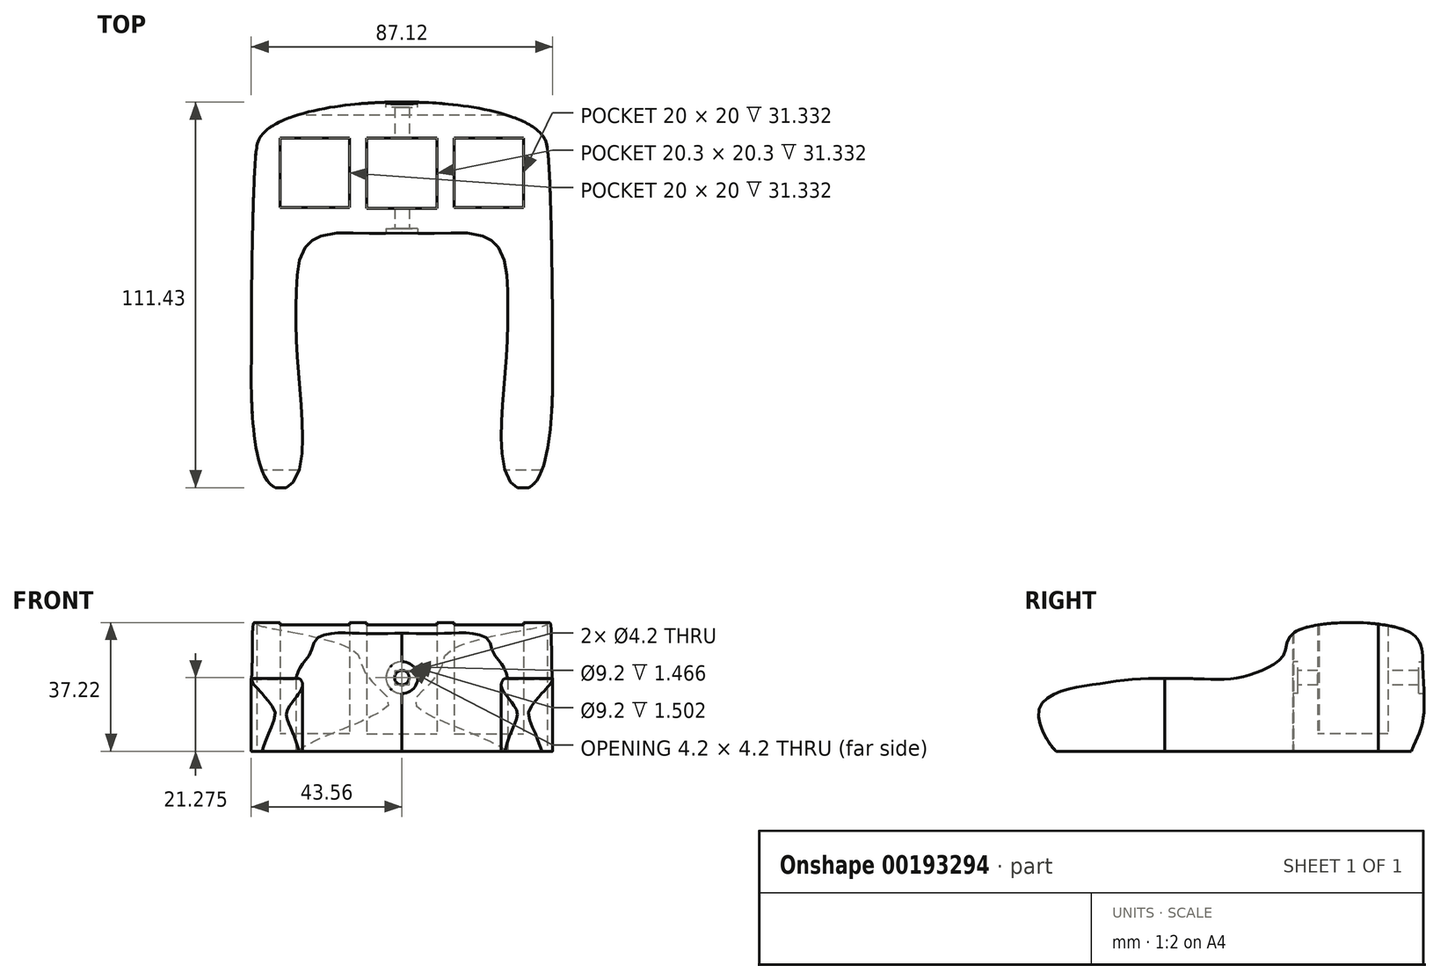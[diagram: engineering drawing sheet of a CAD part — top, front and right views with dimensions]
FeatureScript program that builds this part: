
annotation { "Feature Type Name" : "Feature", "Feature Type Description" : "" }
export const myFeature = defineFeature(function(context is Context, id is Id, definition is map)
    precondition{}
    {
        {
            var Q0;
            Q0=qCreatedBy(makeId("Top.planeOp"),FACE);
            var sketch = newSketch(context, id + "F0", { "sketchPlane" : qUnion([Q0])});
            skLineSegment(sketch, "E0.bottom", {"start": v(-10.15, 48.11) * mm, "end": v(10.15, 48.11) * mm});
            skLineSegment(sketch, "E0.top", {"start": v(-10.15, 27.81) * mm, "end": v(10.15, 27.81) * mm});
            skLineSegment(sketch, "E0.left", {"start": v(-10.15, 48.11) * mm, "end": v(-10.15, 27.81) * mm});
            skLineSegment(sketch, "E0.right", {"start": v(10.15, 48.11) * mm, "end": v(10.15, 27.81) * mm});
            skLineSegment(sketch, "E1.bottom", {"start": v(-15.15, 48.11) * mm, "end": v(-35.15, 48.11) * mm});
            skLineSegment(sketch, "E1.top", {"start": v(-15.15, 28.11) * mm, "end": v(-35.15, 28.11) * mm});
            skLineSegment(sketch, "E1.left", {"start": v(-15.15, 48.11) * mm, "end": v(-15.15, 28.11) * mm});
            skLineSegment(sketch, "E1.right", {"start": v(-35.15, 48.11) * mm, "end": v(-35.15, 28.11) * mm});
            skLineSegment(sketch, "E2.bottom", {"start": v(15.15, 48.11) * mm, "end": v(35.15, 48.11) * mm});
            skLineSegment(sketch, "E2.top", {"start": v(15.15, 28.11) * mm, "end": v(35.15, 28.11) * mm});
            skLineSegment(sketch, "E2.left", {"start": v(15.15, 48.11) * mm, "end": v(15.15, 28.11) * mm});
            skLineSegment(sketch, "E2.right", {"start": v(35.15, 48.11) * mm, "end": v(35.15, 28.11) * mm});
            skFitSpline(sketch, "E3", {"points": [v(-41.99, 45.25) * mm, v(41.99, 45.25) * mm], "startDerivative": vector(1.23, 53.35) * mm, "endDerivative": vector(1.23, -53.35) * mm});
            skFitSpline(sketch, "E4", {"points": [v(-41.99, 45.25) * mm, v(-43.52, -16.46) * mm], "startDerivative": vector(-3.14, -15.96) * mm, "endDerivative": vector(0.23, -65.67) * mm});
            skFitSpline(sketch, "E5.MirrorCS", {"points": [v(41.99, 45.25) * mm, v(43.52, -16.46) * mm], "startDerivative": vector(3.14, -15.96) * mm, "endDerivative": vector(-0.23, -65.67) * mm});
            skFitSpline(sketch, "E6", {"points": [v(0, 20.68) * mm, v(-11.13, 20.58) * mm, v(-20.67, 20.53) * mm, v(-28.24, 16.15) * mm, v(-30.57, 0) * mm, v(-30.07, -17.24) * mm, v(-31.04, -50.84) * mm, v(-38.5, -51.4) * mm, v(-43.52, -16.46) * mm], "startDerivative": vector(-77.7, -4.48) * mm, "endDerivative": vector(3, 147.65) * mm});
            skFitSpline(sketch, "E7.MirrorCS", {"points": [v(0, 20.68) * mm, v(11.13, 20.58) * mm, v(20.67, 20.53) * mm, v(28.24, 16.15) * mm, v(30.57, 0) * mm, v(30.07, -17.24) * mm, v(31.04, -50.84) * mm, v(38.5, -51.4) * mm, v(43.52, -16.46) * mm], "startDerivative": vector(77.7, -4.48) * mm, "endDerivative": vector(-3, 147.65) * mm});
            skPoint(sketch, "E8", {"position": v(0, 58.6) * mm});
            skSolve(sketch);
        }
        {
            var Q0;
            Q0=makeQuery(id+"F0.imprint","IMPRINT",FACE,{"disambiguationData":[TD([[makeQuery(id+"F0.imprint","IMPRINT",EDGE,{"derivedFrom":sQuery(id+"F0.wireOp",EDGE,"E0.bottom")}),1.0]])]});
            extrude(context, id + "F1", {"entities" : qUnion([Q0]), "depth" : 42 * mm});
        }
        {
            var Q0;
            Q0=makeQuery(id+"F0.imprint","IMPRINT",FACE,{"disambiguationData":[TD([[makeQuery(id+"F0.imprint","IMPRINT",EDGE,{"derivedFrom":sQuery(id+"F0.wireOp",EDGE,"E1.bottom")}),1.0]])]});
            var Q1;
            Q1=makeQuery(id+"F0.imprint","IMPRINT",FACE,{"disambiguationData":[TD([[makeQuery(id+"F0.imprint","IMPRINT",EDGE,{"derivedFrom":sQuery(id+"F0.wireOp",EDGE,"E2.bottom")}),-1.0]])]});
            var Q2;
            Q2=makeQuery(id+"F0.imprint","IMPRINT",FACE,{"disambiguationData":[TD([[makeQuery(id+"F0.imprint","IMPRINT",EDGE,{"derivedFrom":sQuery(id+"F0.wireOp",EDGE,"E0.bottom")}),-1.0]])]});
            var Q3;
            Q3=makeQuery(id+"F1.opExtrude","CAP_FACE",FACE,{"disambiguationData":[OSD([sQuery(id+"F0.wireOp",EDGE,"E0.bottom"),sQuery(id+"F0.wireOp",EDGE,"E0.top"),sQuery(id+"F0.wireOp",EDGE,"E0.left"),sQuery(id+"F0.wireOp",EDGE,"E0.right"),sQuery(id+"F0.wireOp",EDGE,"PLPdKNTW-535s-2sd3-3G2i-QsEQIeTVCwCa"),sQuery(id+"F0.wireOp",EDGE,"9fY9yYjP-DSjO-kXnk-1759-b7wDKrXtMASS"),sQuery(id+"F0.wireOp",EDGE,"jWcgoNej-Poc5-GXb6-iVuL-HZIeNCN4XKzx"),sQuery(id+"F0.wireOp",EDGE,"jYB2kJXk-2Wwt-facd-FkQA-iZcFd8I8d0JY"),sQuery(id+"F0.wireOp",EDGE,"umXqAlqO-Gdpm-SvBg-LdQk-NiOLUBJpLZQg"),sQuery(id+"F0.wireOp",EDGE,"xCW1zstU-s8ZH-rEtH-A8zf-q7jx07kdDPo2"),sQuery(id+"F0.wireOp",EDGE,"GzWEVA9t-ngO0-ULYo-wey4-gACoNajw4UZG"),sQuery(id+"F0.wireOp",EDGE,"VOasW8fJ-zNsJ-J5FI-E5Fs-M0nbrpQbyQg6"),sQuery(id+"F0.wireOp",EDGE,"bd66e3c1-5203-4c17-b3e9-319ebe1ef1bb.filletArc"),sQuery(id+"F0.wireOp",EDGE,"45b81584-aca0-4408-9561-ba7d0ac4427e.filletArc"),sQuery(id+"F0.wireOp",EDGE,"13fce822-12cf-430a-b3e8-ab60c30c4311.filletArc"),sQuery(id+"F0.wireOp",EDGE,"26c17914-701f-4d0a-8d2b-51edbc220e85.filletArc"),sQuery(id+"F0.wireOp",EDGE,"80d0b5d1-c0f5-41fd-9bae-3c8ae51292e0.filletArc"),sQuery(id+"F0.wireOp",EDGE,"0f2ecabf-5082-4ff5-bd0e-52d62e53c362.filletArc"),sQuery(id+"F0.wireOp",EDGE,"f6cf3a7c-aae2-4a6d-a22c-1732472adf88.filletArc"),sQuery(id+"F0.wireOp",EDGE,"13254bf5-524f-40b3-8bbc-9e9d387eb92e.filletArc"),sQuery(id+"F0.wireOp",EDGE,"E1.bottom"),sQuery(id+"F0.wireOp",EDGE,"E1.top"),sQuery(id+"F0.wireOp",EDGE,"E1.left"),sQuery(id+"F0.wireOp",EDGE,"E1.right"),sQuery(id+"F0.wireOp",EDGE,"E2.bottom"),sQuery(id+"F0.wireOp",EDGE,"E2.top"),sQuery(id+"F0.wireOp",EDGE,"E2.left"),sQuery(id+"F0.wireOp",EDGE,"E2.right")])],"isStart":false});
            extrude(context, id + "F2", {"entities" : qUnion([Q0, Q1, Q2]), "operationType" : NewBodyOperationType.ADD, "depth" : 5 * mm});
        }
        {
            var Q0;
            Q0=qCreatedBy(makeId("Right.planeOp"),FACE);
            var sketch = newSketch(context, id + "F3", { "sketchPlane" : qUnion([Q0])});
            skFitSpline(sketch, "E9", {"points": [v(-47.83, 0) * mm, v(-52.6, 12.54) * mm, v(-36.61, 19.35) * mm, v(-28.93, 20.42) * mm, v(-22.9, 20.92) * mm, v(-8.29, 21) * mm, v(5.3, 21.33) * mm, v(15.22, 25.27) * mm, v(18.4, 28.85) * mm, v(20.97, 34.35) * mm, v(54.4, 34.35) * mm, v(58.13, 24.55) * mm, v(57.99, 8.04) * mm, v(54.75, 0) * mm], "startDerivative": vector(-71.04, 60.73) * mm, "endDerivative": vector(-29.56, -73.38) * mm});
            skLineSegment(sketch, "E10", {"start": v(-47.83, 0) * mm, "end": v(54.75, 0) * mm});
            skLineSegment(sketch, "E11", {"start": v(20.97, 34.35) * mm, "end": v(54.4, 34.35) * mm});
            skSolve(sketch);
        }
        {
            var Q0;
            Q0 = qSketchRegion(id + "F3", true);
            extrude(context, id + "F4", {"entities" : qUnion([Q0]), "operationType" : NewBodyOperationType.INTERSECT, "endBound" : BoundingType.SYMMETRIC, "depth" : 100.4 * mm});
        }
        {
            var Q0;
            Q0=qCreatedBy(makeId("Front.planeOp"),FACE);
            cPlane(context, id + "F5", {"entities" : qUnion([Q0]), "cplaneType" : CPlaneType.OFFSET, "offset" : 20 * mm, "oppositeDirection" : true, "width" : 150 * mm, "height" : 150 * mm});
        }
        {
            var Q0;
            Q0=qCreatedBy(id+"F5.planeOp",FACE);
            var sketch = newSketch(context, id + "F6", { "sketchPlane" : qUnion([Q0])});
            skLineSegment(sketch, "E12.0", {"start": v(0, 34.15) * mm, "end": v(0, 0) * mm});
            skPoint(sketch, "E13", {"position": v(0, 21.28) * mm});
            skCircle(sketch, "E14", {"center": v(0, 21.28) * mm, "radius": 4.6 * mm});
            skSolve(sketch);
        }
        {
            var Q0;
            Q0=sQuery(id+"F6.wireOp",VERTEX,"E13");
            var Q1;
            Q1=makeQuery(id+"F1.opExtrude","SWEPT_BODY",BODY,{"disambiguationData":[OSD([sQuery(id+"F0.wireOp",EDGE,"E0.bottom"),sQuery(id+"F0.wireOp",EDGE,"E0.top"),sQuery(id+"F0.wireOp",EDGE,"E0.left"),sQuery(id+"F0.wireOp",EDGE,"E0.right"),sQuery(id+"F0.wireOp",EDGE,"E1.bottom"),sQuery(id+"F0.wireOp",EDGE,"E1.top"),sQuery(id+"F0.wireOp",EDGE,"E1.left"),sQuery(id+"F0.wireOp",EDGE,"E1.right"),sQuery(id+"F0.wireOp",EDGE,"E2.bottom"),sQuery(id+"F0.wireOp",EDGE,"E2.top"),sQuery(id+"F0.wireOp",EDGE,"E2.left"),sQuery(id+"F0.wireOp",EDGE,"E2.right"),sQuery(id+"F0.wireOp",EDGE,"E3"),sQuery(id+"F0.wireOp",EDGE,"E4"),sQuery(id+"F0.wireOp",EDGE,"E5.MirrorCS"),sQuery(id+"F0.wireOp",EDGE,"E6"),sQuery(id+"F0.wireOp",EDGE,"E7.MirrorCS")])]});
            hole(context, id + "F7", {"style" : HoleStyle.SIMPLE, "endStyle" : HoleEndStyle.THROUGH, "standardTappedOrClearance" : lookupTablePath({ "standard" : "ISO", "fit" : "Close", "size" : "M4", "type" : "Clearance" }), "standardBlindInLast" : lookupTablePath({ "fit" : "Close", "standard" : "ISO", "size" : "M4", "type" : "Clearance" }), "holeDiameter" : 4.2 * mm, "startFromSketch" : true, "locations" : qUnion([Q0]), "scope" : qUnion([Q1]), "isTappedThrough" : true});
        }
        {
            var Q0;
            {var subQ0=sQuery(id+"F6.wireOp",EDGE,"E14");var subQ1=sQuery(id+"F6.wireOp",EDGE,"E12.0");var subQ2=makeQuery(id+"F6.imprint","INTERSECT",VERTEX,{"disambiguationData":[OD(0.0)],"derivedFrom":[subQ1,subQ0]});Q0=makeQuery(id+"F6.imprint","IMPRINT",FACE,{"disambiguationData":[TD([[makeQuery(id+"F6.imprint","IMPRINT",EDGE,{"disambiguationData":[TD([[subQ2,1.0]])],"derivedFrom":subQ1}),1.0]])]});}
            var Q1;
            {var subQ0=sQuery(id+"F6.wireOp",EDGE,"E14");var subQ1=sQuery(id+"F6.wireOp",EDGE,"E12.0");var subQ2=makeQuery(id+"F6.imprint","INTERSECT",VERTEX,{"disambiguationData":[OD(0.0)],"derivedFrom":[subQ1,subQ0]});Q1=makeQuery(id+"F6.imprint","IMPRINT",FACE,{"disambiguationData":[TD([[makeQuery(id+"F6.imprint","IMPRINT",EDGE,{"disambiguationData":[TD([[subQ2,1.0]])],"derivedFrom":subQ1}),-1.0]])]});}
            var Q2;
            Q2=sQuery(id+"F6.wireOp",EDGE,"E14");
            extrude(context, id + "F8", {"entities" : qUnion([Q0, Q1]), "operationType" : NewBodyOperationType.REMOVE, "surfaceEntities" : qUnion([Q2]), "oppositeDirection" : true, "depth" : 2 * mm});
        }
        {
            var Q0;
            Q0=qCreatedBy(makeId("Front.planeOp"),FACE);
            cPlane(context, id + "F9", {"entities" : qUnion([Q0]), "cplaneType" : CPlaneType.OFFSET, "offset" : 60 * mm, "oppositeDirection" : true, "width" : 150 * mm, "height" : 150 * mm});
        }
        {
            var Q0;
            Q0=qCreatedBy(id+"F9.planeOp",FACE);
            var sketch = newSketch(context, id + "F10", { "sketchPlane" : qUnion([Q0])});
            skCircle(sketch, "E15.0", {"center": v(0, 21.28) * mm, "radius": 2.1 * mm});
            skCircle(sketch, "E16", {"center": v(0, 21.28) * mm, "radius": 4.6 * mm});
            skSolve(sketch);
        }
        {
            var Q0;
            Q0=makeQuery(id+"F10.imprint","IMPRINT",FACE,{"disambiguationData":[TD([[makeQuery(id+"F10.imprint","IMPRINT",EDGE,{"derivedFrom":sQuery(id+"F10.wireOp",EDGE,"E16")}),1.0]])]});
            extrude(context, id + "F11", {"entities" : qUnion([Q0]), "operationType" : NewBodyOperationType.REMOVE, "depth" : 3 * mm});
        }
        {
            var Q0;
            Q0=qCreatedBy(makeId("Top.planeOp"),FACE);
            cPlane(context, id + "F12", {"entities" : qUnion([Q0]), "cplaneType" : CPlaneType.OFFSET, "offset" : 35 * mm, "width" : 150 * mm, "height" : 150 * mm});
        }
    });
